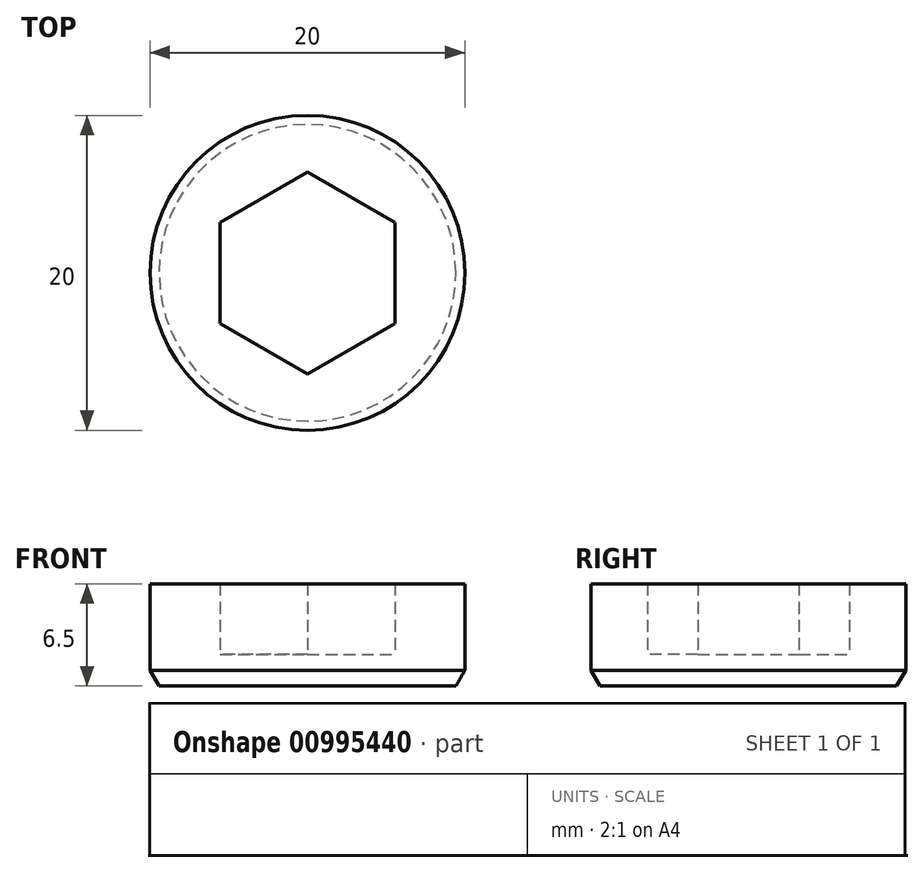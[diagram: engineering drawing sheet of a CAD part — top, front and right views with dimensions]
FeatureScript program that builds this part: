
annotation { "Feature Type Name" : "Feature", "Feature Type Description" : "" }
export const myFeature = defineFeature(function(context is Context, id is Id, definition is map)
    precondition{}
    {
        {
            var Q0;
            Q0=qCreatedBy(makeId("Top.planeOp"),FACE);
            var sketch = newSketch(context, id + "F0", { "sketchPlane" : qUnion([Q0])});
            skCircle(sketch, "E0", {"center": v(0, 0) * mm, "radius": 10 * mm});
            skCircle(sketch, "E1.cCircle", {"center": v(0, 0) * mm, "radius": 5.56 * mm, "construction": true});
            skLineSegment(sketch, "E1.0", {"start": v(-5.56, 3.2) * mm, "end": v(0, 6.42) * mm});
            skLineSegment(sketch, "E1.1", {"start": v(0, 6.42) * mm, "end": v(5.56, 3.2) * mm});
            skLineSegment(sketch, "E1.2", {"start": v(5.56, 3.2) * mm, "end": v(5.56, -3.2) * mm});
            skLineSegment(sketch, "E1.3", {"start": v(5.56, -3.2) * mm, "end": v(0, -6.42) * mm});
            skLineSegment(sketch, "E1.4", {"start": v(0, -6.42) * mm, "end": v(-5.56, -3.2) * mm});
            skLineSegment(sketch, "E1.5", {"start": v(-5.56, -3.2) * mm, "end": v(-5.56, 3.2) * mm});
            skPoint(sketch, "E1.0.midPoint", {"position": v(-2.78, 4.81) * mm});
            skSolve(sketch);
        }
        {
            var Q0;
            Q0 = qSketchRegion(id + "F0", true);
            extrude(context, id + "F1", {"entities" : qUnion([Q0]), "depth" : 6.5 * mm, "offsetDistance" : 25.4 * mm});
        }
        {
            var Q0;
            Q0=makeQuery(id+"F0.imprint","IMPRINT",FACE,{"disambiguationData":[TD([[makeQuery(id+"F0.imprint","IMPRINT",EDGE,{"derivedFrom":sQuery(id+"F0.wireOp",EDGE,"E1.0")}),-1.0]])]});
            extrude(context, id + "F2", {"entities" : qUnion([Q0]), "operationType" : NewBodyOperationType.ADD, "depth" : 2 * mm, "offsetDistance" : 25 * mm});
        }
        {
            var Q0;
            Q0=makeQuery(id+"F1.opExtrude","CAP_EDGE",EDGE,{"disambiguationData":[OSD([sQuery(id+"F0.wireOp",EDGE,"E0")])],"isStart":true});
            chamfer(context, id + "F3", {"entities" : qUnion([Q0]), "chamferType" : ChamferType.OFFSET_ANGLE, "width" : 1 * mm, "oppositeDirection" : false, "angle" : 30 * degree, "tangentPropagation" : true});
        }
    });
